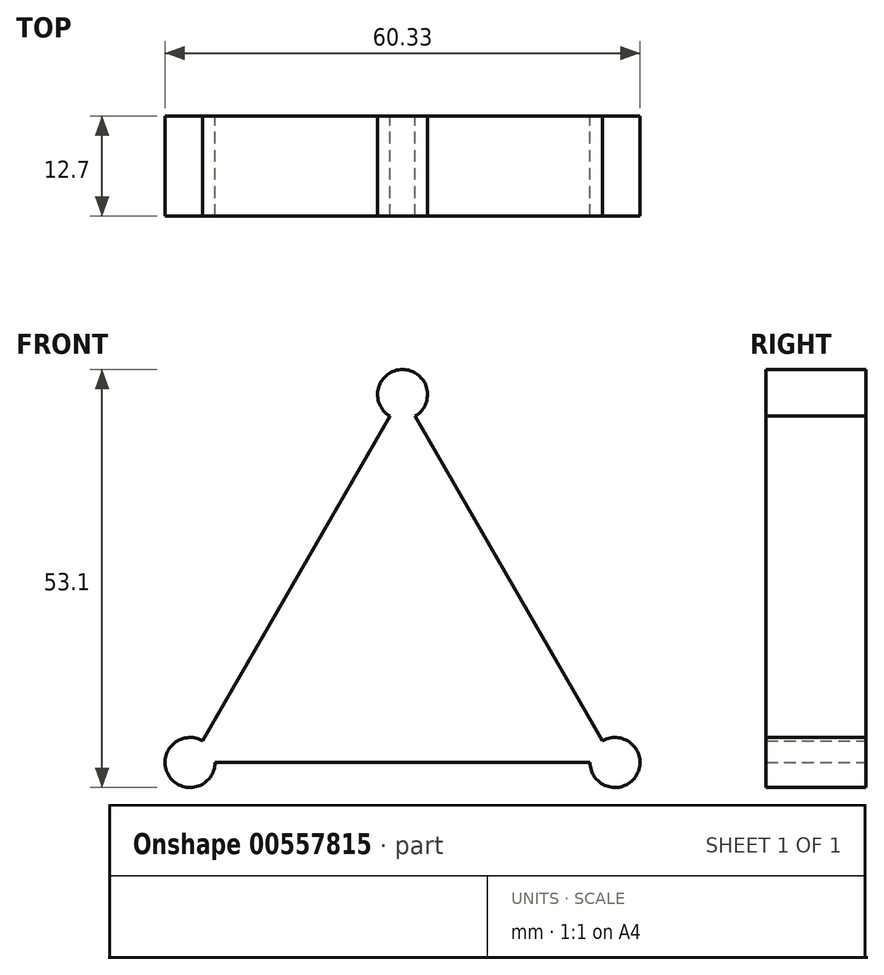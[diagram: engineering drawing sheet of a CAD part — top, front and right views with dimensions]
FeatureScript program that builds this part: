
annotation { "Feature Type Name" : "Feature", "Feature Type Description" : "" }
export const myFeature = defineFeature(function(context is Context, id is Id, definition is map)
    precondition{}
    {
        {
            var Q0;
            Q0=qCreatedBy(makeId("Front.planeOp"),FACE);
            var sketch = newSketch(context, id + "F0", { "sketchPlane" : qUnion([Q0])});
            skCircle(sketch, "E0", {"center": v(26.99, 46.74) * mm, "radius": 3.18 * mm});
            skCircle(sketch, "E1", {"center": v(0, 0) * mm, "radius": 3.18 * mm});
            skCircle(sketch, "E2", {"center": v(53.98, 0) * mm, "radius": 3.18 * mm});
            skLineSegment(sketch, "E3", {"start": v(1.59, 2.75) * mm, "end": v(25.4, 44) * mm});
            skLineSegment(sketch, "E4", {"start": v(28.58, 44) * mm, "end": v(52.39, 2.75) * mm});
            skLineSegment(sketch, "E5", {"start": v(50.8, 0) * mm, "end": v(3.18, 0) * mm});
            skSolve(sketch);
        }
        {
            var Q0;
            Q0 = qSketchRegion(id + "F0", true);
            extrude(context, id + "F1", {"entities" : qUnion([Q0]), "depth" : 12.7 * mm, "offsetDistance" : 25.4 * mm});
        }
    });
